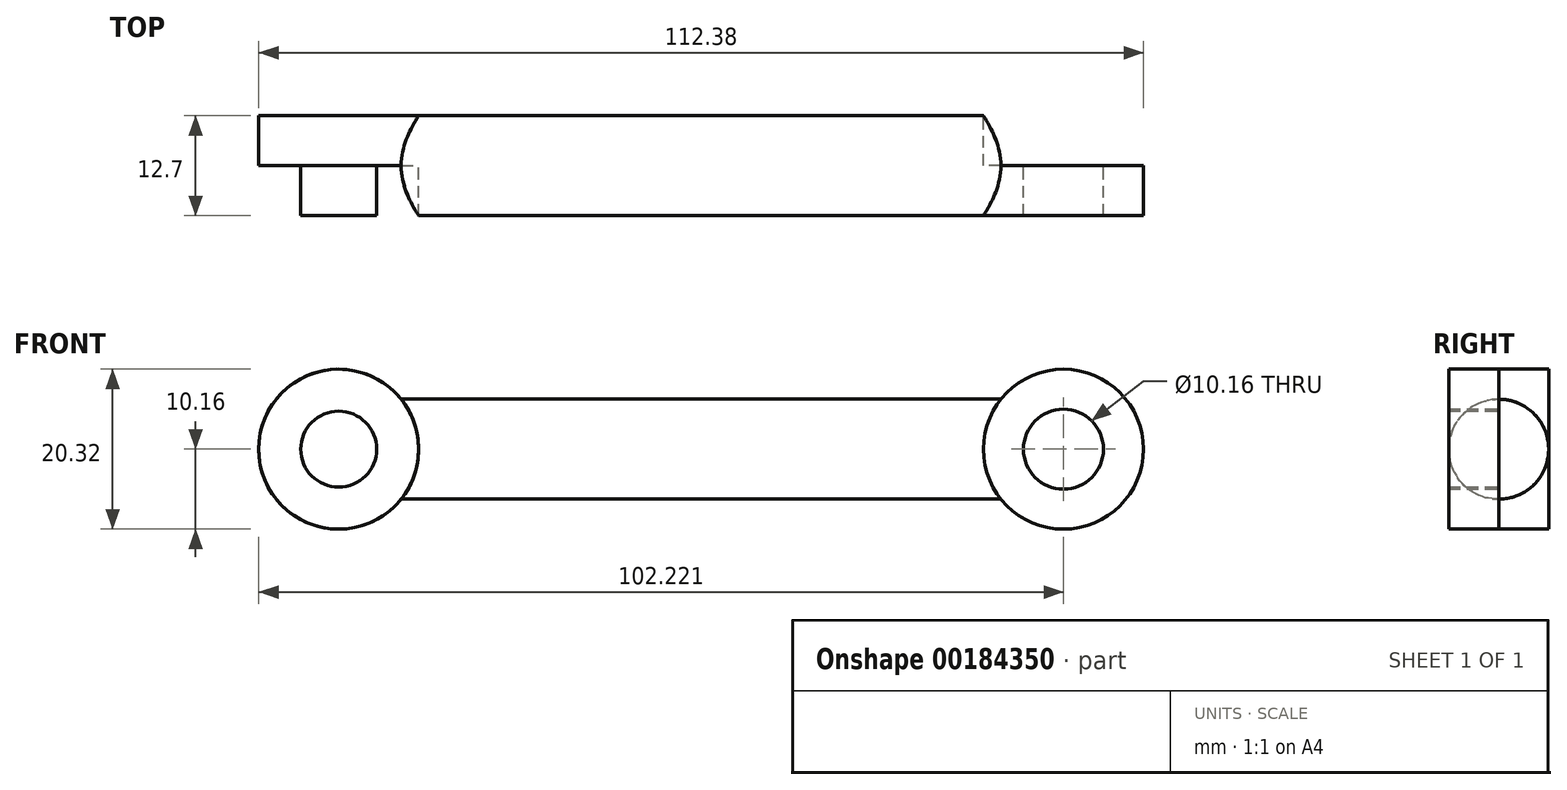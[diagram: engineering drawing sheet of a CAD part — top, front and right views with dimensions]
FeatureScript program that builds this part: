
annotation { "Feature Type Name" : "Feature", "Feature Type Description" : "" }
export const myFeature = defineFeature(function(context is Context, id is Id, definition is map)
    precondition{}
    {
        {
            var Q0;
            Q0=qCreatedBy(makeId("Front.planeOp"),FACE);
            var sketch = newSketch(context, id + "F0", { "sketchPlane" : qUnion([Q0])});
            skLineSegment(sketch, "E0.bottom", {"start": v(-38.1, 6.35) * mm, "end": v(38.1, 6.35) * mm});
            skLineSegment(sketch, "E0.top", {"start": v(-38.1, -6.35) * mm, "end": v(38.1, -6.35) * mm});
            skLineSegment(sketch, "E0.left", {"start": v(-38.1, 6.35) * mm, "end": v(-38.1, -6.35) * mm});
            skLineSegment(sketch, "E0.right", {"start": v(38.1, 6.35) * mm, "end": v(38.1, -6.35) * mm});
            skPoint(sketch, "E0.middle", {"position": v(0, 0) * mm});
            skCircle(sketch, "E1", {"center": v(46.03, 0) * mm, "radius": 10.16 * mm});
            skPoint(sketch, "E1.third.point", {"position": v(56.2, 0) * mm});
            skCircle(sketch, "E2", {"center": v(46.03, 0) * mm, "radius": 5.08 * mm});
            skCircle(sketch, "E3.MirrorC", {"center": v(-46.03, 0) * mm, "radius": 10.16 * mm});
            skCircle(sketch, "E4", {"center": v(-46.03, 0) * mm, "radius": 4.83 * mm});
            skSolve(sketch);
        }
        {
            var Q0;
            {var subQ4=sQuery(id+"F0.wireOp",EDGE,"E0.top");Q0=makeQuery(id+"F0.imprint","IMPRINT",FACE,{"disambiguationData":[TD([[makeQuery(id+"F0.imprint","IMPRINT",EDGE,{"derivedFrom":subQ4}),1.0]])]});}
            var Q1;
            {var subQ0=sQuery(id+"F0.wireOp",EDGE,"E0.left");var subQ1=sQuery(id+"F0.wireOp",EDGE,"E0.bottom");var subQ2=makeQuery(id+"F0.imprint","INTERSECT",VERTEX,{"derivedFrom":[subQ1,subQ0]});Q1=makeQuery(id+"F0.imprint","IMPRINT",FACE,{"disambiguationData":[TD([[makeQuery(id+"F0.imprint","IMPRINT",EDGE,{"disambiguationData":[TD([[subQ2,-1.0]])],"derivedFrom":subQ1}),-1.0]])]});}
            extrude(context, id + "F1", {"entities" : qUnion([Q0, Q1]), "endBound" : BoundingType.SYMMETRIC, "depth" : 12.7 * mm});
        }
        {
            var Q0;
            Q0=makeQuery(id+"F1.opExtrude","CAP_EDGE",EDGE,{"disambiguationData":[OSD([sQuery(id+"F0.wireOp",EDGE,"E0.bottom")])],"isStart":false});
            var Q1;
            Q1=makeQuery(id+"F1.opExtrude","CAP_EDGE",EDGE,{"disambiguationData":[OSD([sQuery(id+"F0.wireOp",EDGE,"E0.bottom")])],"isStart":true});
            var Q2;
            Q2=makeQuery(id+"F1.opExtrude","CAP_EDGE",EDGE,{"disambiguationData":[OSD([sQuery(id+"F0.wireOp",EDGE,"E0.top")])],"isStart":false});
            var Q3;
            Q3=makeQuery(id+"F1.opExtrude","CAP_EDGE",EDGE,{"disambiguationData":[OSD([sQuery(id+"F0.wireOp",EDGE,"E0.top")])],"isStart":true});
            fillet(context, id + "F2", {"entities" : qUnion([Q0, Q1, Q2, Q3]), "radius" : 6.35 * mm, "tangentPropagation" : true, "allowEdgeOverflow" : false});
        }
        {
            var Q0;
            {var subQ0=sQuery(id+"F0.wireOp",EDGE,"E0.right");Q0=makeQuery(id+"F0.imprint","IMPRINT",FACE,{"disambiguationData":[TD([[makeQuery(id+"F0.imprint","IMPRINT",EDGE,{"derivedFrom":subQ0}),-1.0]])]});}
            var Q1;
            {var subQ0=sQuery(id+"F0.wireOp",EDGE,"E0.right");Q1=makeQuery(id+"F0.imprint","IMPRINT",FACE,{"disambiguationData":[TD([[makeQuery(id+"F0.imprint","IMPRINT",EDGE,{"derivedFrom":subQ0}),1.0]])]});}
            extrude(context, id + "F3", {"entities" : qUnion([Q0, Q1]), "operationType" : NewBodyOperationType.ADD, "depth" : 6.35 * mm});
        }
        {
            var Q0;
            {var subQ0=sQuery(id+"F0.wireOp",EDGE,"E0.left");Q0=makeQuery(id+"F0.imprint","IMPRINT",FACE,{"disambiguationData":[TD([[makeQuery(id+"F0.imprint","IMPRINT",EDGE,{"derivedFrom":subQ0}),-1.0]])]});}
            var Q1;
            {var subQ0=sQuery(id+"F0.wireOp",EDGE,"E0.left");Q1=makeQuery(id+"F0.imprint","IMPRINT",FACE,{"disambiguationData":[TD([[makeQuery(id+"F0.imprint","IMPRINT",EDGE,{"derivedFrom":subQ0}),1.0]])]});}
            extrude(context, id + "F4", {"entities" : qUnion([Q0, Q1]), "operationType" : NewBodyOperationType.ADD, "oppositeDirection" : true, "depth" : 6.35 * mm});
        }
        {
            var Q0;
            Q0=makeQuery(id+"F0.imprint","IMPRINT",FACE,{"disambiguationData":[TD([[makeQuery(id+"F0.imprint","IMPRINT",EDGE,{"derivedFrom":sQuery(id+"F0.wireOp",EDGE,"E4")}),1.0]])]});
            extrude(context, id + "F5", {"entities" : qUnion([Q0]), "operationType" : NewBodyOperationType.ADD, "endBound" : BoundingType.SYMMETRIC, "depth" : 12.7 * mm});
        }
    });
